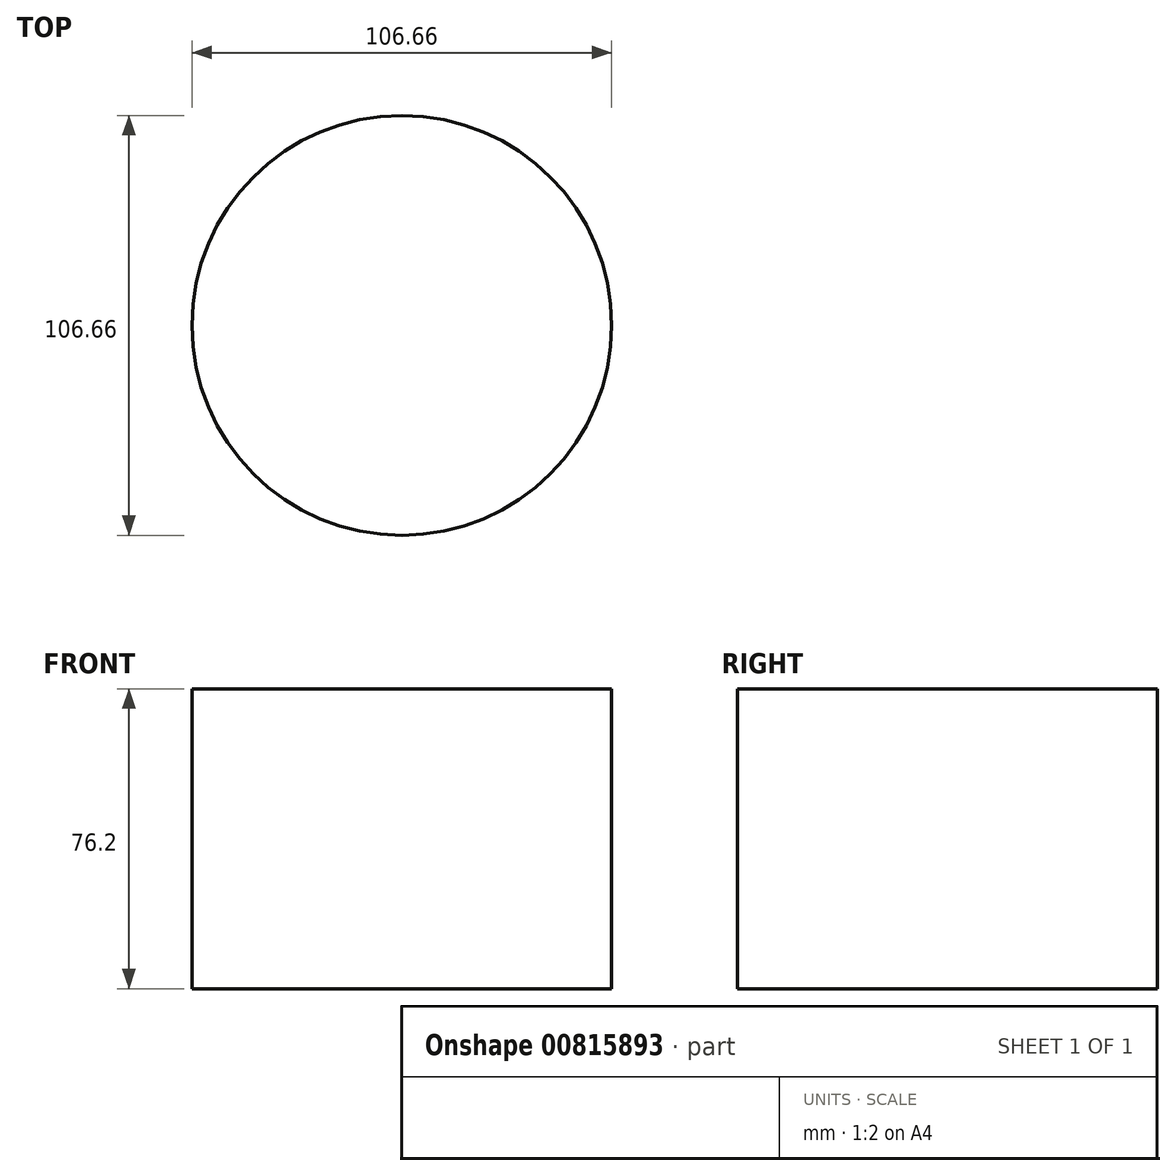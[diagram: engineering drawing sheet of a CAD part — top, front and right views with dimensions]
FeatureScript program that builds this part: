
annotation { "Feature Type Name" : "Feature", "Feature Type Description" : "" }
export const myFeature = defineFeature(function(context is Context, id is Id, definition is map)
    precondition{}
    {
        {
            var Q0;
            Q0=qCreatedBy(makeId("Top.planeOp"),FACE);
            var sketch = newSketch(context, id + "F0", { "sketchPlane" : qUnion([Q0])});
            skCircle(sketch, "E0", {"center": v(0, 0) * mm, "radius": 53.33 * mm});
            skSolve(sketch);
        }
        {
            var Q0;
            Q0=makeQuery(id+"F0.imprint","IMPRINT",FACE,{"disambiguationData":[TD([[makeQuery(id+"F0.imprint","IMPRINT",EDGE,{"derivedFrom":sQuery(id+"F0.wireOp",EDGE,"E0")}),1.0]])]});
            extrude(context, id + "F1", {"entities" : qUnion([Q0]), "endBound" : BoundingType.SYMMETRIC, "depth" : 76.2 * mm, "offsetDistance" : 25.4 * mm});
        }
    });
